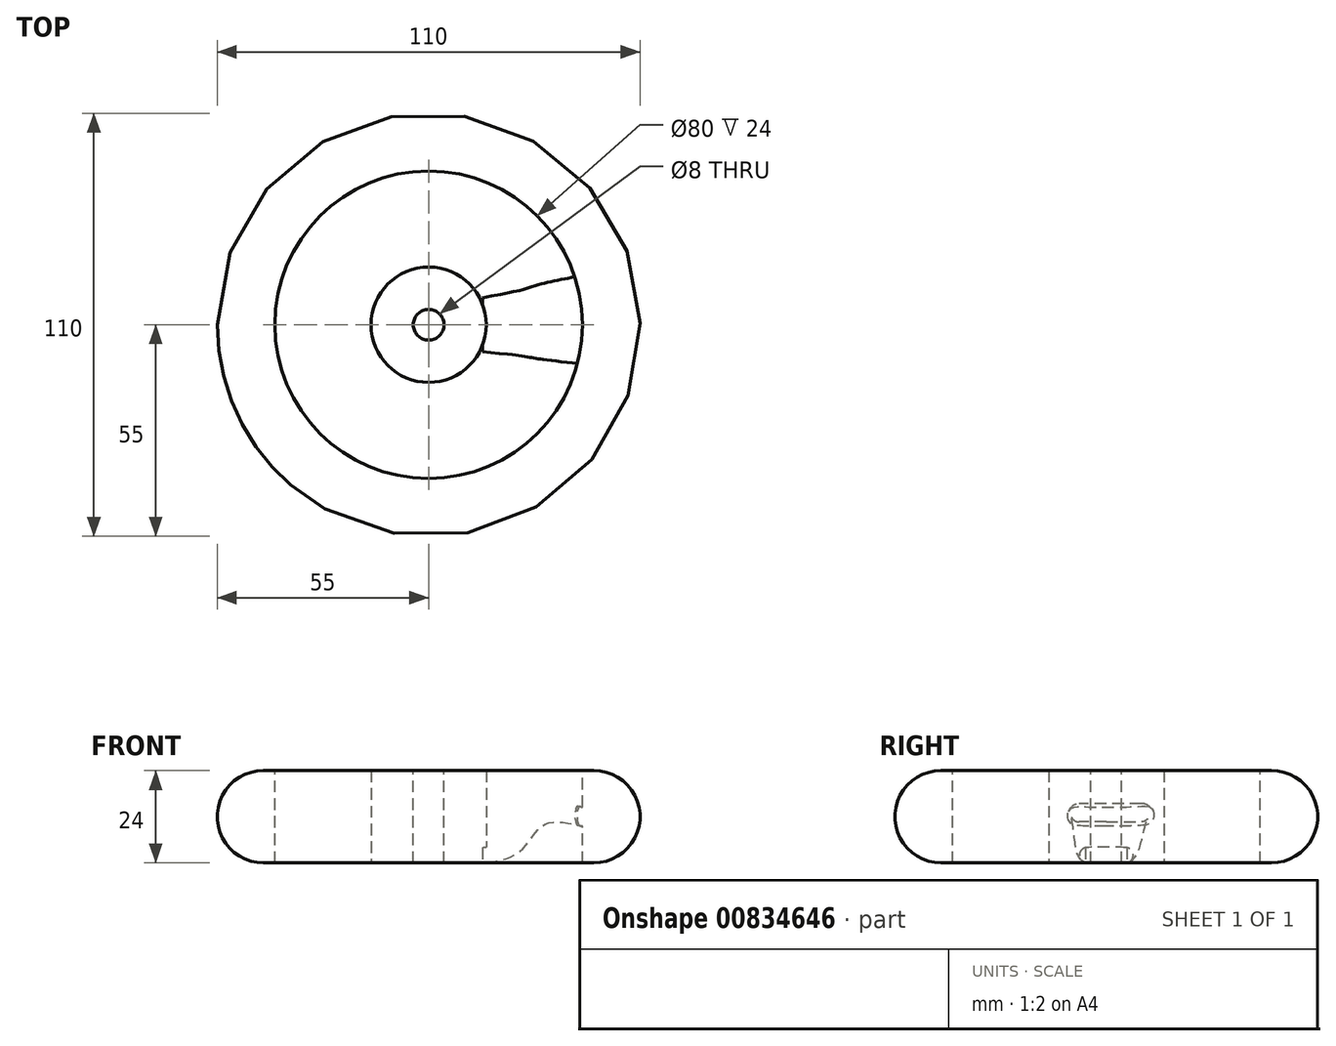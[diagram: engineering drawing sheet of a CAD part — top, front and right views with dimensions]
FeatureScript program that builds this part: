
annotation { "Feature Type Name" : "Feature", "Feature Type Description" : "" }
export const myFeature = defineFeature(function(context is Context, id is Id, definition is map)
    precondition{}
    {
        {
            var Q0;
            Q0=qCreatedBy(makeId("Top.planeOp"),FACE);
            var sketch = newSketch(context, id + "F0", { "sketchPlane" : qUnion([Q0])});
            skCircle(sketch, "E0", {"center": v(0, 0) * mm, "radius": 40 * mm});
            skSolve(sketch);
        }
        {
            var Q0;
            Q0=qCreatedBy(makeId("Front.planeOp"),FACE);
            var sketch = newSketch(context, id + "F1", { "sketchPlane" : qUnion([Q0])});
            skArc(sketch, "E1", {"start": v(-43, 12) * mm, "mid": v(-55, 0) * mm, "end": v(-43, -12) * mm});
            skLineSegment(sketch, "E2", {"start": v(-43, 12) * mm, "end": v(-40, 12) * mm});
            skLineSegment(sketch, "E3", {"start": v(-43, -12) * mm, "end": v(-40, -12) * mm});
            skLineSegment(sketch, "E4", {"start": v(-40, -12) * mm, "end": v(-40, 12) * mm});
            skSolve(sketch);
        }
        {
            var Q0;
            Q0 = qSketchRegion(id + "F1", true);
            var Q1;
            Q1 = qConstructionFilter(qBodyType(qCreatedBy(id + "F0" ,EDGE), BodyType.WIRE), ConstructionObject.NO);
            sweep(context, id + "F2", {"profiles" : qUnion([Q0]), "path" : qUnion([Q1])});
        }
        {
            var Q0;
            Q0=qCreatedBy(makeId("Right.planeOp"),FACE);
            cPlane(context, id + "F3", {"entities" : qUnion([Q0]), "cplaneType" : CPlaneType.OFFSET, "offset" : 40 * mm, "width" : 150 * mm, "height" : 150 * mm});
        }
        {
            var Q0;
            Q0=qCreatedBy(id+"F3.planeOp",FACE);
            var sketch = newSketch(context, id + "F4", { "sketchPlane" : qUnion([Q0])});
            skLineSegment(sketch, "E5", {"start": v(-7.68, 0) * mm, "end": v(10.32, 0) * mm});
            skArc(sketch, "E6.0.startCap", {"start": v(-7.68, -2.5) * mm, "mid": v(-10.18, 0) * mm, "end": v(-7.68, 2.5) * mm});
            skArc(sketch, "E6.0.endCap", {"start": v(10.32, 2.5) * mm, "mid": v(12.82, 0) * mm, "end": v(10.32, -2.5) * mm});
            skLineSegment(sketch, "E6.0.left", {"start": v(-7.68, 2.5) * mm, "end": v(10.32, 2.5) * mm});
            skLineSegment(sketch, "E6.0.right", {"start": v(-7.68, -2.5) * mm, "end": v(10.32, -2.5) * mm});
            skSolve(sketch);
        }
        {
            var Q0;
            Q0=qCreatedBy(makeId("Right.planeOp"),FACE);
            cPlane(context, id + "F5", {"entities" : qUnion([Q0]), "cplaneType" : CPlaneType.OFFSET, "offset" : 14 * mm, "width" : 150 * mm, "height" : 150 * mm});
        }
        {
            var Q0;
            Q0=qCreatedBy(id+"F5.planeOp",FACE);
            var sketch = newSketch(context, id + "F6", { "sketchPlane" : qUnion([Q0])});
            skLineSegment(sketch, "E7", {"start": v(-5, -10) * mm, "end": v(5, -10) * mm});
            skArc(sketch, "E8.0.startCap", {"start": v(-5, -12) * mm, "mid": v(-7, -10) * mm, "end": v(-5, -8) * mm});
            skArc(sketch, "E8.0.endCap", {"start": v(5, -8) * mm, "mid": v(7, -10) * mm, "end": v(5, -12) * mm});
            skLineSegment(sketch, "E8.0.left", {"start": v(-5, -8) * mm, "end": v(5, -8) * mm});
            skLineSegment(sketch, "E8.0.right", {"start": v(-5, -12) * mm, "end": v(5, -12) * mm});
            skSolve(sketch);
        }
        {
            var Q0;
            Q0=qCreatedBy(makeId("Front.planeOp"),FACE);
            var sketch = newSketch(context, id + "F7", { "sketchPlane" : qUnion([Q0])});
            skFitSpline(sketch, "E9", {"points": [v(14, -12) * mm, v(23.93, -8.85) * mm, v(30.35, -1.9) * mm, v(40, -2.5) * mm], "startDerivative": vector(27.89, 1.32) * mm, "endDerivative": vector(27.75, -6.41) * mm});
            skSolve(sketch);
        }
        {
            var Q1;
            Q1 = qSketchRegion(id + "F6", true);
            var Q2;
            Q2 = qSketchRegion(id + "F4", true);
            var Q3;
            Q3 = qConstructionFilter(qBodyType(qCreatedBy(id + "F7" ,EDGE), BodyType.WIRE), ConstructionObject.NO);
            loft(context, id + "F8", {"operationType" : NewBodyOperationType.ADD, "addGuides" : true, "sheetProfilesArray" : [{ "sheetProfileEntities" : qUnion([Q1]) }, { "sheetProfileEntities" : qUnion([Q2]) }], "guidesArray" : [{ "guideEntities" : qUnion([Q3]), "guideDerivativeType" : LoftGuideDerivativeType.DEFAULT, "guideDerivativeMagnitude" : 1 }]});
        }
        {
            var Q0;
            Q0=qCreatedBy(makeId("Front.planeOp"),FACE);
            var sketch = newSketch(context, id + "F9", { "sketchPlane" : qUnion([Q0])});
            skLineSegment(sketch, "E10", {"start": v(0, 12) * mm, "end": v(15, 12) * mm});
            skLineSegment(sketch, "E11", {"start": v(15, 12) * mm, "end": v(15, -12) * mm});
            skLineSegment(sketch, "E12", {"start": v(15, -12) * mm, "end": v(0, -12) * mm});
            skLineSegment(sketch, "E13", {"start": v(0, -12) * mm, "end": v(0, 12) * mm});
            skSolve(sketch);
        }
        {
            var Q0;
            Q0 = qSketchRegion(id + "F9", true);
            var Q1;
            Q1=sQuery(id+"F9.wireOp",EDGE,"E13");
            revolve(context, id + "F10", {"operationType" : NewBodyOperationType.ADD, "surfaceOperationType" : NewSurfaceOperationType.NEW, "entities" : qUnion([Q0]), "axis" : qUnion([Q1]), "revolveType" : RevolveType.FULL});
        }
        {
            var Q0;
            Q0=makeQuery(id+"F10.opRevolve","SWEPT_FACE",FACE,{"disambiguationData":[OSD([sQuery(id+"F9.wireOp",EDGE,"E10")])]});
            var sketch = newSketch(context, id + "F11", { "sketchPlane" : qUnion([Q0])});
            skPoint(sketch, "E14", {"position": v(0, 0) * mm});
            skSolve(sketch);
        }
        {
            var Q0;
            Q0=sQuery(id+"F11.wireOp",VERTEX,"E14");
            var Q1;
            Q1=makeQuery(id+"F2.opSweep","SWEPT_BODY",BODY,{"disambiguationData":[OSD([sQuery(id+"F0.wireOp",EDGE,"E0"),sQuery(id+"F1.wireOp",EDGE,"E1"),sQuery(id+"F1.wireOp",EDGE,"E2"),sQuery(id+"F1.wireOp",EDGE,"E3"),sQuery(id+"F1.wireOp",EDGE,"E4")])]});
            hole(context, id + "F12", {"style" : HoleStyle.SIMPLE, "endStyle" : HoleEndStyle.THROUGH, "holeDiameter" : 8 * mm, "majorDiameter" : 5 * mm, "isTappedThrough" : true, "tappedDepth" : 12 * mm, "tapClearance" : 3, "locations" : qUnion([Q0]), "scope" : qUnion([Q1])});
        }
    });
